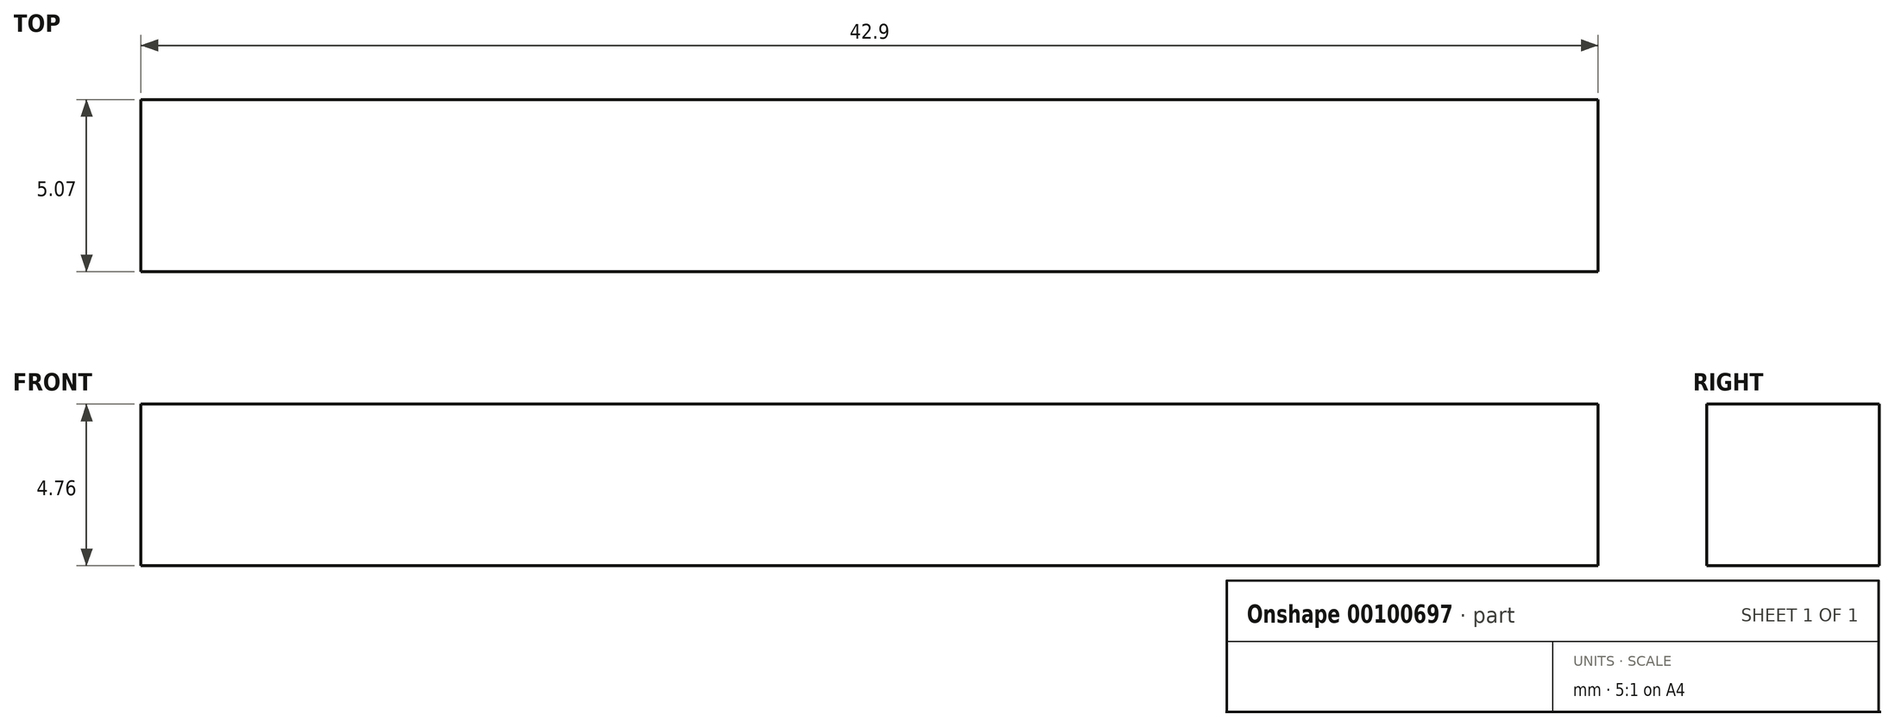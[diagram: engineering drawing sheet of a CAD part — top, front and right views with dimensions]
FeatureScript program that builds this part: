
annotation { "Feature Type Name" : "Feature", "Feature Type Description" : "" }
export const myFeature = defineFeature(function(context is Context, id is Id, definition is map)
    precondition{}
    {
        {
            var Q0;
            Q0=qCreatedBy(makeId("Front.planeOp"),FACE);
            var sketch = newSketch(context, id + "F0", { "sketchPlane" : qUnion([Q0])});
            skLineSegment(sketch, "E0.bottom", {"start": v(21.45, -2.38) * mm, "end": v(-21.45, -2.38) * mm});
            skLineSegment(sketch, "E0.top", {"start": v(21.45, 2.38) * mm, "end": v(-21.45, 2.38) * mm});
            skLineSegment(sketch, "E0.left", {"start": v(21.45, -2.38) * mm, "end": v(21.45, 2.38) * mm});
            skLineSegment(sketch, "E0.right", {"start": v(-21.45, -2.38) * mm, "end": v(-21.45, 2.38) * mm});
            skPoint(sketch, "E0.middle", {"position": v(0, 0) * mm});
            skSolve(sketch);
        }
        {
            var Q0;
            Q0 = qSketchRegion(id + "F0", true);
            extrude(context, id + "F1", {"entities" : qUnion([Q0]), "depth" : 5.07 * mm});
        }
    });
